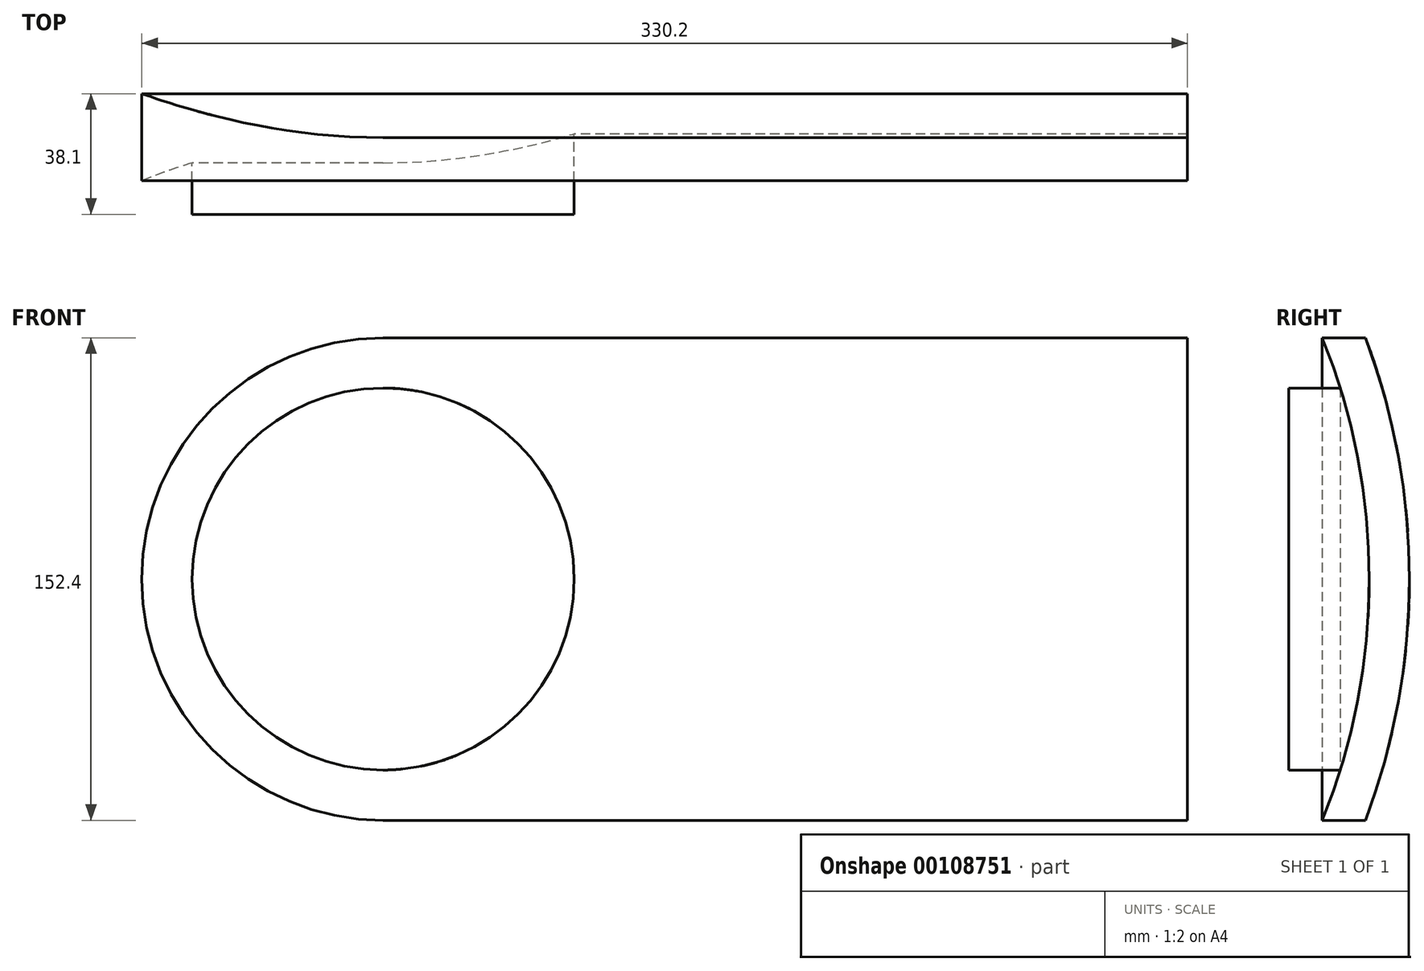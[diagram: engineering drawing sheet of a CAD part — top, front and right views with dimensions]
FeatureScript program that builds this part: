
annotation { "Feature Type Name" : "Feature", "Feature Type Description" : "" }
export const myFeature = defineFeature(function(context is Context, id is Id, definition is map)
    precondition{}
    {
        {
            var Q0;
            Q0=qCreatedBy(makeId("Front.planeOp"),FACE);
            var sketch = newSketch(context, id + "F0", { "sketchPlane" : qUnion([Q0])});
            skCircle(sketch, "E0", {"center": v(0, 0) * mm, "radius": 60.33 * mm});
            skArc(sketch, "E1", {"start": v(0, 76.2) * mm, "mid": v(-76.2, 0) * mm, "end": v(0, -76.2) * mm});
            skLineSegment(sketch, "E2", {"start": v(0, 76.2) * mm, "end": v(254, 76.2) * mm});
            skLineSegment(sketch, "E3", {"start": v(254, 76.2) * mm, "end": v(254, -76.2) * mm});
            skLineSegment(sketch, "E4", {"start": v(0, -76.2) * mm, "end": v(254, -76.2) * mm});
            skSolve(sketch);
        }
        {
            var Q0;
            Q0=makeQuery(id+"F0.imprint","IMPRINT",FACE,{"disambiguationData":[TD([[makeQuery(id+"F0.imprint","IMPRINT",EDGE,{"derivedFrom":sQuery(id+"F0.wireOp",EDGE,"E0")}),-1.0]])]});
            var Q1;
            Q1=makeQuery(id+"F0.imprint","IMPRINT",FACE,{"disambiguationData":[TD([[makeQuery(id+"F0.imprint","IMPRINT",EDGE,{"derivedFrom":sQuery(id+"F0.wireOp",EDGE,"E0")}),1.0]])]});
            extrude(context, id + "F1", {"entities" : qUnion([Q0, Q1]), "endBound" : BoundingType.SYMMETRIC, "depth" : 38.1 * mm});
        }
        {
            var Q0;
            Q0=qCreatedBy(makeId("Right.planeOp"),FACE);
            var sketch = newSketch(context, id + "F2", { "sketchPlane" : qUnion([Q0])});
            skLineSegment(sketch, "E5", {"start": v(0, 0) * mm, "end": v(-203.2, 0) * mm, "construction": true});
            skCircle(sketch, "E6", {"center": v(-203.2, 0) * mm, "radius": 203.2 * mm});
            skArc(sketch, "E7", {"start": v(-18.26, -111.4) * mm, "mid": v(12.64, -5.06) * mm, "end": v(-13.24, 102.6) * mm});
            skLineSegment(sketch, "E8", {"start": v(-13.24, 102.6) * mm, "end": v(114.28, 102.6) * mm});
            skLineSegment(sketch, "E9", {"start": v(114.28, 102.6) * mm, "end": v(114.28, -111.4) * mm});
            skLineSegment(sketch, "E10", {"start": v(114.28, -111.4) * mm, "end": v(-18.26, -111.4) * mm});
            skSolve(sketch);
        }
        {
            var Q0;
            Q0=makeQuery(id+"F2.imprint","IMPRINT",FACE,{"disambiguationData":[TD([[makeQuery(id+"F2.imprint","IMPRINT",EDGE,{"derivedFrom":sQuery(id+"F2.wireOp",EDGE,"E6")}),1.0]])]});
            var sketch = newSketch(context, id + "F3", { "sketchPlane" : qUnion([Q0])});
            skArc(sketch, "E11", {"start": v(0, 0) * mm, "mid": v(-203.2, 203.2) * mm, "end": v(-406.4, 0) * mm});
            skLineSegment(sketch, "E12", {"start": v(-406.4, 0) * mm, "end": v(0, 0) * mm});
            skSolve(sketch);
        }
        {
            var Q0;
            Q0 = qSketchRegion(id + "F3", true);
            var Q1;
            Q1=sQuery(id+"F3.wireOp",EDGE,"E12");
            revolve(context, id + "F4", {"operationType" : NewBodyOperationType.REMOVE, "entities" : qUnion([Q0]), "axis" : qUnion([Q1]), "revolveType" : RevolveType.ONE_DIRECTION, "oppositeDirection" : true, "angle" : 180 * degree});
        }
        {
            var Q0;
            Q0=makeQuery(id+"F2.imprint","IMPRINT",FACE,{"disambiguationData":[TD([[makeQuery(id+"F2.imprint","IMPRINT",EDGE,{"derivedFrom":sQuery(id+"F2.wireOp",EDGE,"E6")}),1.0]])]});
            extrude(context, id + "F5", {"entities" : qUnion([Q0]), "operationType" : NewBodyOperationType.REMOVE, "depth" : 492.65 * mm});
        }
        {
            var Q0;
            Q0=makeQuery(id+"F2.imprint","IMPRINT",FACE,{"disambiguationData":[TD([[makeQuery(id+"F2.imprint","IMPRINT",EDGE,{"derivedFrom":sQuery(id+"F2.wireOp",EDGE,"E7")}),-1.0]])]});
            extrude(context, id + "F6", {"entities" : qUnion([Q0]), "operationType" : NewBodyOperationType.REMOVE, "endBound" : BoundingType.SYMMETRIC, "oppositeDirection" : true, "depth" : 571.72 * mm});
        }
        {
            var Q0;
            Q0=makeQuery(id+"F0.imprint","IMPRINT",FACE,{"disambiguationData":[TD([[makeQuery(id+"F0.imprint","IMPRINT",EDGE,{"derivedFrom":sQuery(id+"F0.wireOp",EDGE,"E0")}),1.0]])]});
            extrude(context, id + "F7", {"entities" : qUnion([Q0]), "operationType" : NewBodyOperationType.ADD, "depth" : 25.4 * mm});
        }
    });
